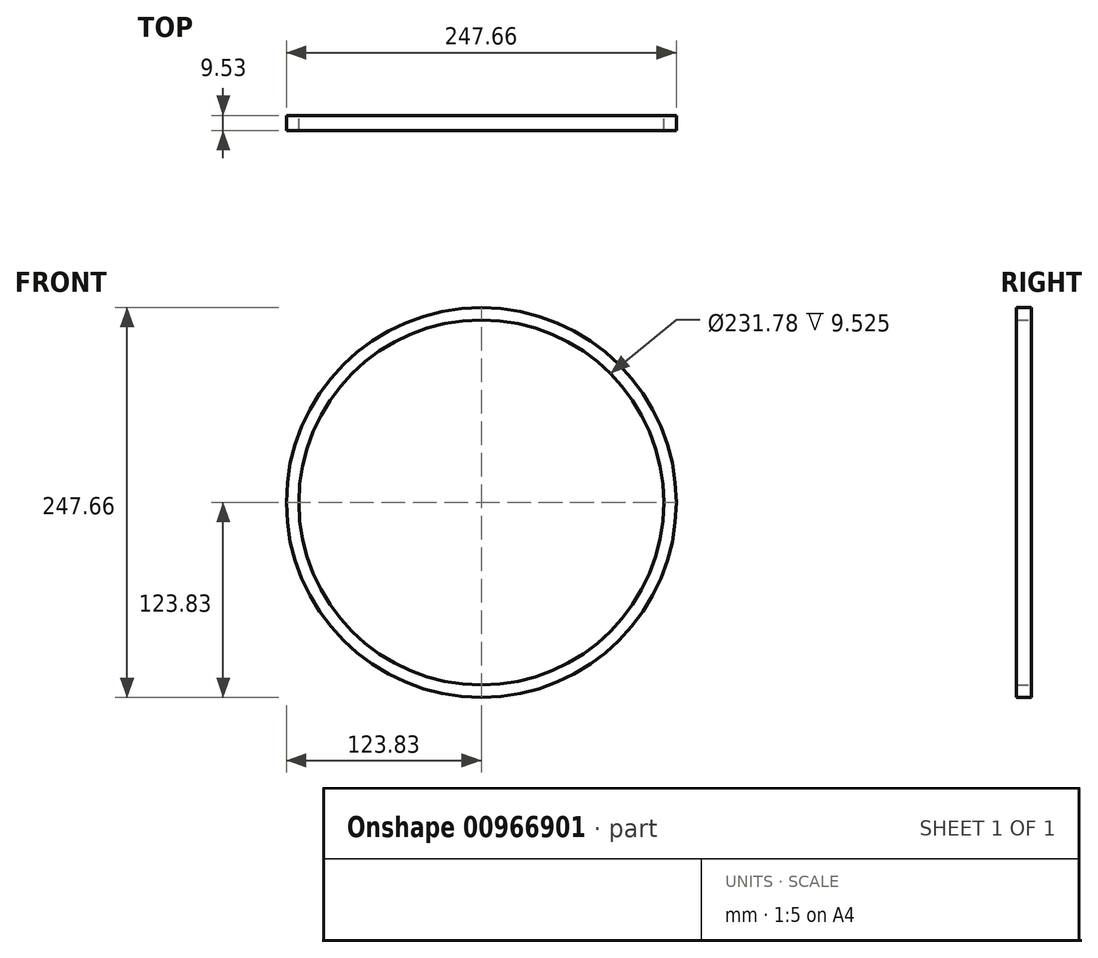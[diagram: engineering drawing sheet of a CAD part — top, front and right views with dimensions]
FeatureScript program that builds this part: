
annotation { "Feature Type Name" : "Feature", "Feature Type Description" : "" }
export const myFeature = defineFeature(function(context is Context, id is Id, definition is map)
    precondition{}
    {
        {
            var Q0;
            Q0=qCreatedBy(makeId("Front.planeOp"),FACE);
            var sketch = newSketch(context, id + "F0", { "sketchPlane" : qUnion([Q0])});
            skCircle(sketch, "E0", {"center": v(0, 0) * mm, "radius": 123.83 * mm});
            skCircle(sketch, "E1.0", {"center": v(0, 0) * mm, "radius": 115.89 * mm});
            skSolve(sketch);
        }
        {
            var Q0;
            Q0 = qSketchRegion(id + "F0", true);
            extrude(context, id + "F1", {"entities" : qUnion([Q0]), "depth" : 9.52 * mm, "offsetDistance" : 25.4 * mm});
        }
    });
